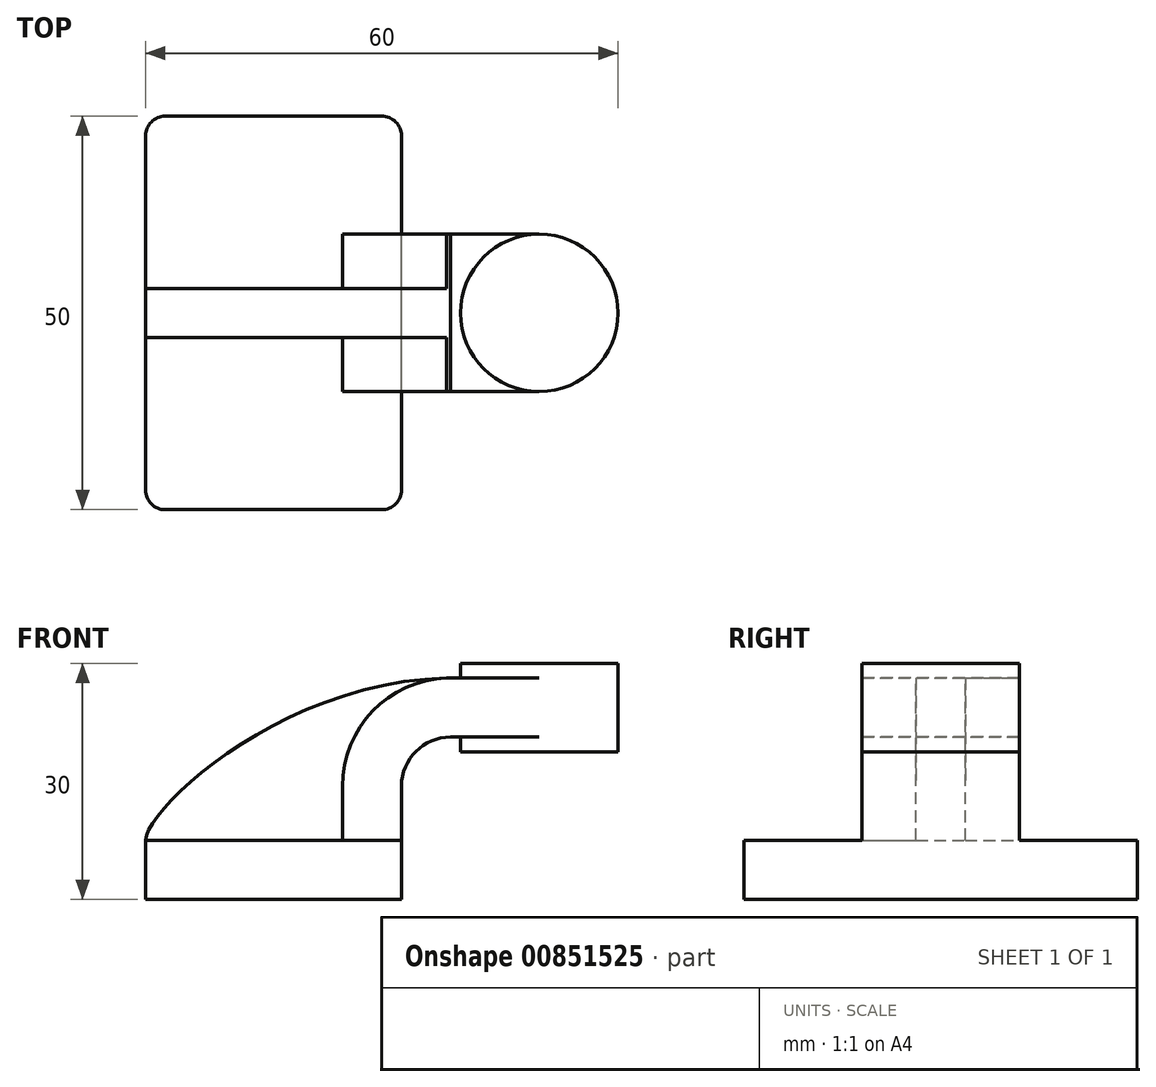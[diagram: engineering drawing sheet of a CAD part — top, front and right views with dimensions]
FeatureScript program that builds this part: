
annotation { "Feature Type Name" : "Feature", "Feature Type Description" : "" }
export const myFeature = defineFeature(function(context is Context, id is Id, definition is map)
    precondition{}
    {
        {
            var Q0;
            Q0=qCreatedBy(makeId("Front.planeOp"),FACE);
            var sketch = newSketch(context, id + "F0", { "sketchPlane" : qUnion([Q0])});
            skLineSegment(sketch, "E0.bottom", {"start": v(16.25, 3.75) * mm, "end": v(-16.25, 3.75) * mm});
            skLineSegment(sketch, "E0.top", {"start": v(16.25, -3.75) * mm, "end": v(-16.25, -3.75) * mm});
            skLineSegment(sketch, "E0.left", {"start": v(16.25, 3.75) * mm, "end": v(16.25, -3.75) * mm});
            skLineSegment(sketch, "E0.right", {"start": v(-16.25, 3.75) * mm, "end": v(-16.25, -3.75) * mm});
            skPoint(sketch, "E0.middle", {"position": v(0, 0) * mm});
            skLineSegment(sketch, "E1.bottom", {"start": v(43.75, 26.25) * mm, "end": v(23.75, 26.25) * mm});
            skLineSegment(sketch, "E1.top", {"start": v(43.75, 15) * mm, "end": v(23.75, 15) * mm});
            skLineSegment(sketch, "E1.left", {"start": v(43.75, 26.25) * mm, "end": v(43.75, 15) * mm});
            skLineSegment(sketch, "E1.right", {"start": v(23.75, 26.25) * mm, "end": v(23.75, 15) * mm});
            skPoint(sketch, "E1.middle", {"position": v(33.75, 20.63) * mm});
            skLineSegment(sketch, "E2", {"start": v(16.25, 3.75) * mm, "end": v(16.25, 10.63) * mm});
            skArc(sketch, "E3", {"start": v(16.25, 10.63) * mm, "mid": v(18.08, 15.05) * mm, "end": v(22.5, 16.88) * mm});
            skLineSegment(sketch, "E4", {"start": v(22.5, 16.88) * mm, "end": v(33.75, 16.88) * mm});
            skLineSegment(sketch, "E5.0", {"start": v(22.5, 24.38) * mm, "end": v(33.75, 24.38) * mm});
            skArc(sketch, "E5.1", {"start": v(8.75, 10.63) * mm, "mid": v(12.78, 20.35) * mm, "end": v(22.5, 24.38) * mm});
            skLineSegment(sketch, "E5.2", {"start": v(8.75, 3.75) * mm, "end": v(8.75, 10.63) * mm});
            skFitSpline(sketch, "E6", {"points": [v(-16.25, 3.75) * mm, v(22.5, 24.38) * mm], "startDerivative": vector(0.37, 12.34) * mm, "endDerivative": vector(64.09, 0.79) * mm});
            skLineSegment(sketch, "E7", {"start": v(33.75, 26.25) * mm, "end": v(33.75, 15) * mm});
            skPoint(sketch, "E8", {"position": v(33.75, 15) * mm});
            skSolve(sketch);
        }
        {
            var Q0;
            Q0=makeQuery(id+"F0.imprint","IMPRINT",FACE,{"disambiguationData":[TD([[makeQuery(id+"F0.imprint","IMPRINT",EDGE,{"derivedFrom":sQuery(id+"F0.wireOp",EDGE,"E0.top")}),-1.0]])]});
            extrude(context, id + "F1", {"entities" : qUnion([Q0]), "endBound" : BoundingType.SYMMETRIC, "depth" : 50 * mm, "offsetDistance" : 25 * mm});
        }
        {
            var Q0;
            {var subQ6=sQuery(id+"F0.wireOp",EDGE,"E2");Q0=makeQuery(id+"F0.imprint","IMPRINT",FACE,{"disambiguationData":[TD([[makeQuery(id+"F0.imprint","IMPRINT",EDGE,{"derivedFrom":subQ6}),1.0]])]});}
            var Q1;
            {var subQ5=sQuery(id+"F0.wireOp",EDGE,"3EGpEISf-sQFq-PsbW-uCY8-kqpqayrGWiVZ");Q1=makeQuery(id+"F0.imprint","IMPRINT",FACE,{"disambiguationData":[TD([[makeQuery(id+"F0.imprint","IMPRINT",EDGE,{"derivedFrom":subQ5}),-1.0]])]});}
            var Q2;
            {var subQ0=sQuery(id+"F0.wireOp",EDGE,"E5.0");var subQ1=sQuery(id+"F0.wireOp",EDGE,"E1.right");var subQ2=makeQuery(id+"F0.imprint","INTERSECT",VERTEX,{"derivedFrom":[subQ1,subQ0]});Q2=makeQuery(id+"F0.imprint","IMPRINT",FACE,{"disambiguationData":[TD([[makeQuery(id+"F0.imprint","IMPRINT",EDGE,{"disambiguationData":[TD([[subQ2,-1.0]])],"derivedFrom":subQ1}),1.0]])]});}
            extrude(context, id + "F2", {"entities" : qUnion([Q0, Q1, Q2]), "operationType" : NewBodyOperationType.ADD, "endBound" : BoundingType.SYMMETRIC, "depth" : 20 * mm, "offsetDistance" : 25 * mm});
        }
        {
            var Q0;
            {var subQ3=sQuery(id+"F0.wireOp",EDGE,"E5.2");Q0=makeQuery(id+"F0.imprint","IMPRINT",FACE,{"disambiguationData":[TD([[makeQuery(id+"F0.imprint","IMPRINT",EDGE,{"derivedFrom":subQ3}),1.0]])]});}
            extrude(context, id + "F3", {"entities" : qUnion([Q0]), "operationType" : NewBodyOperationType.ADD, "endBound" : BoundingType.SYMMETRIC, "depth" : 6.25 * mm, "offsetDistance" : 25 * mm});
        }
        {
            var Q0;
            {var subQ4=sQuery(id+"F0.wireOp",EDGE,"E1.left");Q0=makeQuery(id+"F0.imprint","IMPRINT",FACE,{"disambiguationData":[TD([[makeQuery(id+"F0.imprint","IMPRINT",EDGE,{"derivedFrom":subQ4}),-1.0]])]});}
            var Q1;
            Q1=sQuery(id+"F0.wireOp",EDGE,"E7");
            revolve(context, id + "F4", {"operationType" : NewBodyOperationType.ADD, "surfaceOperationType" : NewSurfaceOperationType.NEW, "entities" : qUnion([Q0]), "axis" : qUnion([Q1]), "revolveType" : RevolveType.FULL});
        }
        {
            var Q0;
            Q0=makeQuery(id+"F1.opExtrude","CAP_EDGE",EDGE,{"disambiguationData":[OSD([sQuery(id+"F0.wireOp",EDGE,"E0.right")])],"isStart":false});
            var Q1;
            Q1=makeQuery(id+"F1.opExtrude","CAP_EDGE",EDGE,{"disambiguationData":[OSD([sQuery(id+"F0.wireOp",EDGE,"E0.left")])],"isStart":false});
            var Q2;
            Q2=makeQuery(id+"F1.opExtrude","CAP_EDGE",EDGE,{"disambiguationData":[OSD([sQuery(id+"F0.wireOp",EDGE,"E0.right")])],"isStart":true});
            var Q3;
            Q3=makeQuery(id+"F1.opExtrude","CAP_EDGE",EDGE,{"disambiguationData":[OSD([sQuery(id+"F0.wireOp",EDGE,"E0.left")])],"isStart":true});
            fillet(context, id + "F5", {"entities" : qUnion([Q0, Q1, Q2, Q3]), "radius" : 2.5 * mm, "tangentPropagation" : true, "allowEdgeOverflow" : false});
        }
    });
